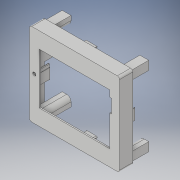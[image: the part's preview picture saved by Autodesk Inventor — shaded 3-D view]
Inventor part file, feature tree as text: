
AUTODESK INVENTOR PART (.ipt)
format: ipt  version: 2019 (Build 230136000, 136)  size: 654,848 bytes
history: native  units: mm
features: other x9, extrude x9, sketch x3, hole x1, fillet x1, projected_geometry x1
ambient origin geometry x8: Origin, YZ Plane, XZ Plane, XY Plane, X Axis, Y Axis, Z Axis, Center Point
bodies: Solid1 (feature_tree)
feature tree (24):
  other  "case_top"
  extrude  "Extrusion1"  Depth=72.0mm
  extrude  "Extrusion2"  Depth=7.0mm
  other  "resetTL_zarez_vedeni"
  extrude  "Extrusion3"  Depth=64.2mm
  extrude  "Extrusion4"  Depth=5.8mm
  extrude  "Extrusion7"  Depth=1.5mm
  hole  "Hole1"  [1 undecoded]
  extrude  "Extrusion8"  Depth=1.5mm
  extrude  "Extrusion9"  Depth=23.15mm
  extrude  "Extrusion10"  Depth=0.8mm
  fillet  "Fillet1"  Radius=3.0mm
  extrude  "Extrusion11"  Depth=4.5mm
  other  "vrsek"
  other  "displej_vyrez"
  other  "resetTL_vnitrek_vybrani"
  other  "resetTL_dira"
  other  "spojeni_srouby"
  other  "diry_zavitova_vlozka"
  sketch  "Sketch10"  dims[d0=78.5mm d1=72.0mm]
  projected_geometry  "Projected Loop1"
  other  "dira_RJ45"
  sketch  "Sketch12"  dims[d2=1.2mm d3=0.0mm d4=7.0mm]
  sketch  "Sketch13"  dims[d5=23.15mm d6=64.2mm d7=5.8mm d8=1.5mm d9=12.4mm d10=1.5mm d11=23.15mm d12=36.0mm d13=3.0mm d14=0.0mm d15=4.5mm d16=7.0mm d19=2.0mm d20=21.0mm d21=0.9mm d22=0.0mm d23=3.0mm d24=2.0mm d25=0.0mm d45=8.0mm d47=26.5mm d48=0.0mm d49=3.3mm d50=6.0mm d51=3.75mm d52=2.0mm d53=1.745329mm d54=12.0mm d55=0.0mm d56=0.4mm d57=0.0mm d58=2.5mm d59=0.4mm d60=0.0mm d61=1.6mm d62=16.8mm d64=0.0mm d65=17.3mm d66=1.6mm d67=0.0mm d68=0.0mm d70=10.5mm d71=1.6mm d72=0.0mm d73=0.0mm d74=15.45mm d75=2.0mm d76=1.2mm d77=10.0mm d79=0.0mm d80=0.8mm d81=0.4mm d82=10.0mm d83=1.2mm d84=0.0mm d86=0.0mm d87=0.8mm d89=10.0mm d90=1.2mm d91=0.0mm d92=0.0mm d93=1.2mm d94=10.0mm d95=0.0mm d96=0.0mm d97=0.8mm d98=14.0mm d99=1.0mm d100=0.0mm d101=0.0mm d106=31.15mm d107=4.2mm d108=7.0mm d109=0.8mm]
note: 1 required parameter value undecoded (feature->parameter linkage not recoverable at this tier; creation-order binding heuristic only, values carry confidence <= 0.55)
